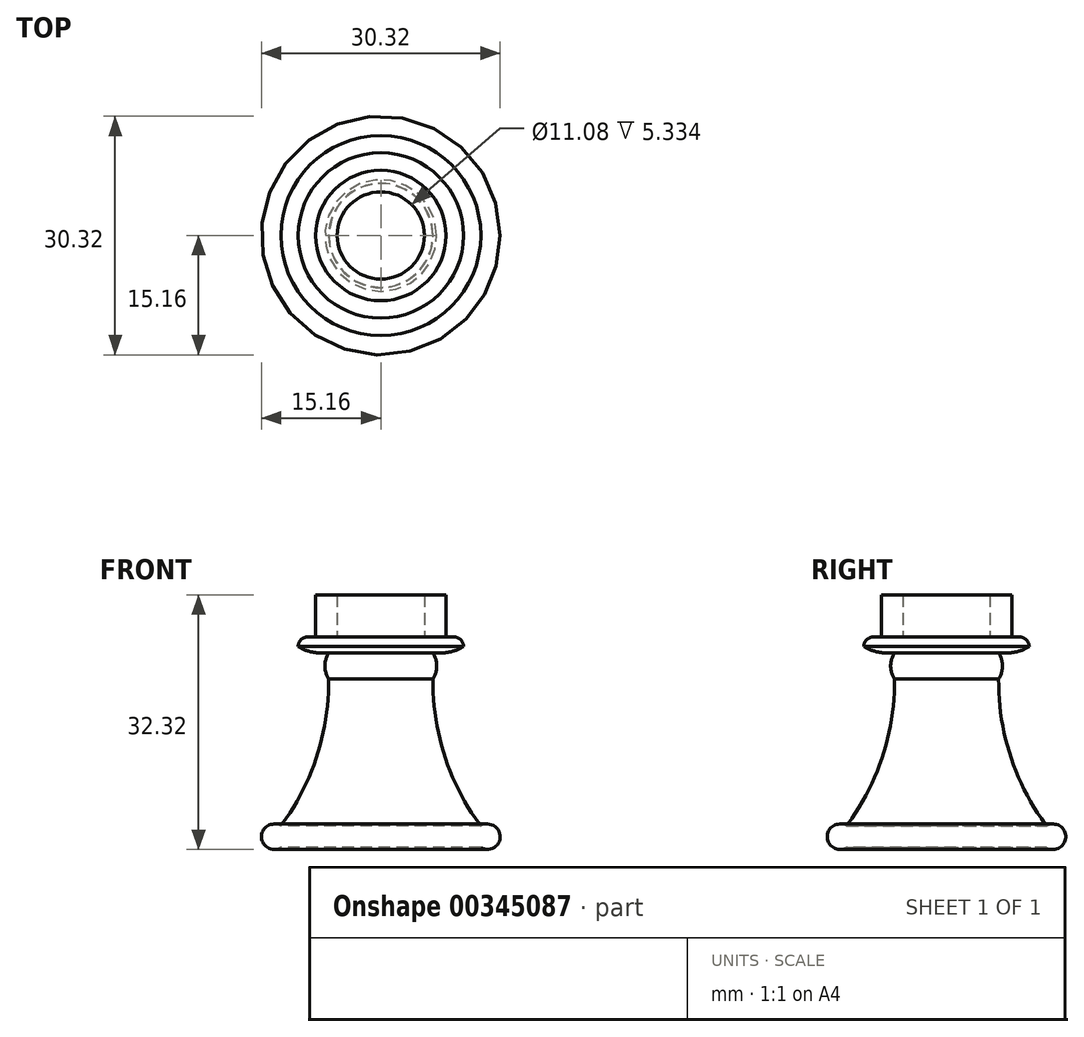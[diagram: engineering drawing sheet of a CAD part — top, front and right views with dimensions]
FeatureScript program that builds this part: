
annotation { "Feature Type Name" : "Feature", "Feature Type Description" : "" }
export const myFeature = defineFeature(function(context is Context, id is Id, definition is map)
    precondition{}
    {
        {
            var Q0;
            Q0=qCreatedBy(makeId("Front.planeOp"),FACE);
            var sketch = newSketch(context, id + "F0", { "sketchPlane" : qUnion([Q0])});
            skLineSegment(sketch, "E0", {"start": v(0, 0) * mm, "end": v(12.7, 0) * mm});
            skArc(sketch, "E1", {"start": v(12.7, 0) * mm, "mid": v(15.16, 1.36) * mm, "end": v(12.7, 2.72) * mm});
            skLineSegment(sketch, "E2", {"start": v(0, 24.7) * mm, "end": v(0, 0) * mm});
            skPoint(sketch, "E3.start.orphan", {"position": v(9.45, 21.63) * mm});
            skPoint(sketch, "E4.start.orphan", {"position": v(9.45, 24.7) * mm});
            skArc(sketch, "E5", {"start": v(6.62, 21.4) * mm, "mid": v(8.13, 11.56) * mm, "end": v(12.7, 2.72) * mm});
            skArc(sketch, "E6", {"start": v(6.62, 21.4) * mm, "mid": v(7.1, 23.05) * mm, "end": v(6.62, 24.7) * mm});
            skLineSegment(sketch, "E7", {"start": v(6.62, 24.7) * mm, "end": v(0, 24.7) * mm});
            skSolve(sketch);
        }
        {
            var Q0;
            Q0 = qSketchRegion(id + "F0", true);
            var Q1;
            Q1=sQuery(id+"F0.wireOp",EDGE,"E2");
            revolve(context, id + "F1", {"entities" : qUnion([Q0]), "axis" : qUnion([Q1]), "revolveType" : RevolveType.FULL});
        }
        {
            var Q0;
            Q0=makeQuery(id+"F1.opRevolve","SWEPT_FACE",FACE,{"disambiguationData":[OSD([sQuery(id+"F0.wireOp",EDGE,"E7")])]});
            var sketch = newSketch(context, id + "F2", { "sketchPlane" : qUnion([Q0])});
            skCircle(sketch, "E8", {"center": v(0, 0) * mm, "radius": 10.5 * mm});
            skSolve(sketch);
        }
        {
            var Q0;
            Q0 = qSketchRegion(id + "F2", true);
            extrude(context, id + "F3", {"entities" : qUnion([Q0]), "operationType" : NewBodyOperationType.ADD, "depth" : 2.03 * mm});
        }
        {
            var Q0;
            Q0=makeQuery(id+"F3.opExtrude","CAP_EDGE",EDGE,{"disambiguationData":[OSD([sQuery(id+"F2.wireOp",EDGE,"E8")])],"isStart":false});
            fillet(context, id + "F4", {"entities" : qUnion([Q0]), "radius" : 1.23 * mm, "tangentPropagation" : true, "allowEdgeOverflow" : false});
        }
        {
            var Q0;
            Q0=makeQuery(id+"F3.opExtrude","CAP_EDGE",EDGE,{"disambiguationData":[OSD([sQuery(id+"F2.wireOp",EDGE,"E8")])],"isStart":true});
            fillet(context, id + "F5", {"entities" : qUnion([Q0]), "radius" : 5.52 * mm, "tangentPropagation" : true, "allowEdgeOverflow" : false});
        }
        {
            var Q0;
            Q0=makeQuery(id+"F3.opExtrude","CAP_FACE",FACE,{"disambiguationData":[OSD([sQuery(id+"F2.wireOp",EDGE,"E8")])],"isStart":false});
            var sketch = newSketch(context, id + "F6", { "sketchPlane" : qUnion([Q0])});
            skCircle(sketch, "E9", {"center": v(0, 0) * mm, "radius": 8.28 * mm});
            skCircle(sketch, "E10", {"center": v(0, 0) * mm, "radius": 5.54 * mm});
            skSolve(sketch);
        }
        {
            var Q0;
            Q0 = qSketchRegion(id + "F6", true);
            extrude(context, id + "F7", {"entities" : qUnion([Q0]), "operationType" : NewBodyOperationType.ADD, "depth" : 5.33 * mm});
        }
    });
